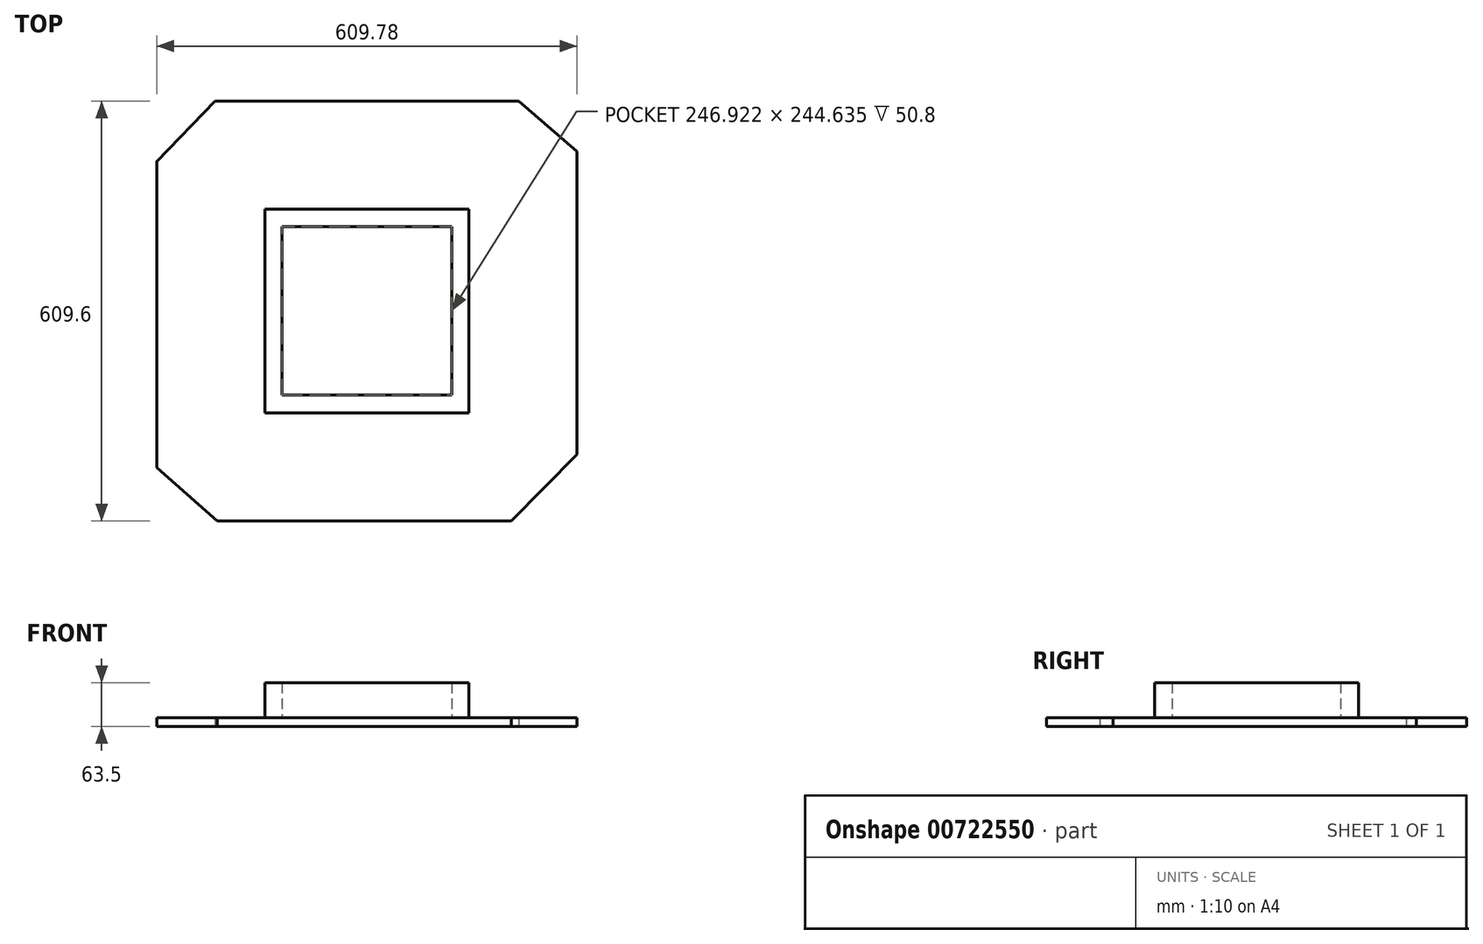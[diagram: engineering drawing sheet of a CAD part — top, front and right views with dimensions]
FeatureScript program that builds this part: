
annotation { "Feature Type Name" : "Feature", "Feature Type Description" : "" }
export const myFeature = defineFeature(function(context is Context, id is Id, definition is map)
    precondition{}
    {
        {
            var Q0;
            Q0=qCreatedBy(makeId("Top.planeOp"),FACE);
            var sketch = newSketch(context, id + "F0", { "sketchPlane" : qUnion([Q0])});
            skLineSegment(sketch, "E0.bottom", {"start": v(220.46, 304.8) * mm, "end": v(-220.21, 304.8) * mm});
            skLineSegment(sketch, "E0.top", {"start": v(209.79, -304.8) * mm, "end": v(-216.9, -304.8) * mm});
            skLineSegment(sketch, "E0.left", {"start": v(304.8, 231.87) * mm, "end": v(304.8, -208.26) * mm});
            skLineSegment(sketch, "E0.right", {"start": v(-304.8, 217.58) * mm, "end": v(-304.8, -227.37) * mm});
            skPoint(sketch, "E0.middle", {"position": v(0, 0) * mm});
            skLineSegment(sketch, "E1", {"start": v(-304.98, 217.4) * mm, "end": v(-304.8, 217.56) * mm});
            skLineSegment(sketch, "E2", {"start": v(-216.9, -304.8) * mm, "end": v(-304.8, -227.37) * mm});
            skLineSegment(sketch, "E3", {"start": v(220.46, 304.8) * mm, "end": v(304.8, 231.87) * mm});
            skLineSegment(sketch, "E4", {"start": v(209.79, -304.8) * mm, "end": v(304.8, -208.26) * mm});
            skLineSegment(sketch, "E5", {"start": v(-304.98, 217.4) * mm, "end": v(-220.21, 304.8) * mm});
            skSolve(sketch);
        }
        {
            var Q0;
            Q0 = qSketchRegion(id + "F0", true);
            extrude(context, id + "F1", {"entities" : qUnion([Q0]), "depth" : 12.7 * mm, "offsetDistance" : 25.4 * mm});
        }
        {
            var Q0;
            Q0=makeQuery(id+"F1.opExtrude","CAP_FACE",FACE,{"disambiguationData":[OSD([sQuery(id+"F0.wireOp",EDGE,"E0.bottom"),sQuery(id+"F0.wireOp",EDGE,"E0.top"),sQuery(id+"F0.wireOp",EDGE,"E0.left"),sQuery(id+"F0.wireOp",EDGE,"E0.right"),sQuery(id+"F0.wireOp",EDGE,"E1"),sQuery(id+"F0.wireOp",EDGE,"E2"),sQuery(id+"F0.wireOp",EDGE,"E3"),sQuery(id+"F0.wireOp",EDGE,"E4"),sQuery(id+"F0.wireOp",EDGE,"E5")])],"isStart":false});
            var sketch = newSketch(context, id + "F2", { "sketchPlane" : qUnion([Q0])});
            skLineSegment(sketch, "E6", {"start": v(-220.21, 304.8) * mm, "end": v(-216.9, -304.8) * mm});
            skLineSegment(sketch, "E7", {"start": v(-124.73, -304.8) * mm, "end": v(-124.73, 304.8) * mm});
            skLineSegment(sketch, "E8", {"start": v(-24.16, 304.8) * mm, "end": v(-24.16, -304.8) * mm});
            skLineSegment(sketch, "E9", {"start": v(67.12, 304.8) * mm, "end": v(67.12, -304.8) * mm});
            skLineSegment(sketch, "E10", {"start": v(151.3, 304.8) * mm, "end": v(151.3, -304.8) * mm});
            skLineSegment(sketch, "E11", {"start": v(220.46, 304.8) * mm, "end": v(220.46, -293.95) * mm});
            skSolve(sketch);
        }
        {
            var Q0;
            {var subQ0=sQuery(id+"F2.wireOp",EDGE,"E11");Q0=makeQuery(id+"F2.imprint","IMPRINT",FACE,{"disambiguationData":[TD([[makeQuery(id+"F2.imprint","IMPRINT",EDGE,{"derivedFrom":subQ0}),1.0]])]});}
            var sketch = newSketch(context, id + "F3", { "sketchPlane" : qUnion([Q0])});
            skLineSegment(sketch, "E12.bottom", {"start": v(147.77, 148.1) * mm, "end": v(-147.77, 148.1) * mm});
            skLineSegment(sketch, "E12.top", {"start": v(147.77, -148.1) * mm, "end": v(-147.77, -148.1) * mm});
            skLineSegment(sketch, "E12.left", {"start": v(147.77, 148.1) * mm, "end": v(147.77, -148.1) * mm});
            skLineSegment(sketch, "E12.right", {"start": v(-147.77, 148.1) * mm, "end": v(-147.77, -148.1) * mm});
            skPoint(sketch, "E12.middle", {"position": v(0, 0) * mm});
            skLineSegment(sketch, "E13.bottom", {"start": v(123.46, 122.32) * mm, "end": v(-123.46, 122.32) * mm});
            skLineSegment(sketch, "E13.top", {"start": v(123.46, -122.32) * mm, "end": v(-123.46, -122.32) * mm});
            skLineSegment(sketch, "E13.left", {"start": v(123.46, 122.32) * mm, "end": v(123.46, -122.32) * mm});
            skLineSegment(sketch, "E13.right", {"start": v(-123.46, 122.32) * mm, "end": v(-123.46, -122.32) * mm});
            skSolve(sketch);
        }
        {
            var Q0;
            Q0 = qSketchRegion(id + "F3", true);
            extrude(context, id + "F4", {"entities" : qUnion([Q0]), "operationType" : NewBodyOperationType.ADD, "depth" : 50.8 * mm, "offsetDistance" : 25.4 * mm});
        }
    });
